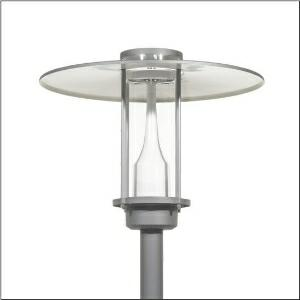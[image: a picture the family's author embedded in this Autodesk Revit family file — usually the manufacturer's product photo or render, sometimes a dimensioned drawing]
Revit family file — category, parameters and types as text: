
# Revit family: city-light_plus_iq___pl1_2s_5xa5275jf14h_3179
name_source: partatom
category: Lighting Fixtures
units: mm (PartAtom-declared; Revit-internal decimal feet)

## family parameters
Cut with Voids When Loaded = No
Host = Face
Light Source = No
Part Type = Normal
Room Calculation Point = No
Round Connector Dimension = Use Diameter
Shared = No

## types (1)
- --- (1 x LED, 2830 lm, 19.3 W, 3000K)
    Apparent Load = 19 VA
    CIE Flux Codes = 23 63 93 97 100
    Color Rendering = 70
    Color Temperature = 3000K
    Default Elevation = 1800 mm
    Description = City-Light Plus iQ, mast luminaire, Module 540 iQ-SR, primary light control with 3 zone facetted reflector, of plastic, silver coated, highly specular, structured, primary optical cover: cover, of PMMA, transparent, light distribution: PL1.2s, light emission: direct distribution, primary light characteristic: symmetric, installation type: post-top, LED, High Power LED, rated luminous flux: 2.830lm, luminous efficacy: 146lm/W, light colour: 730, colour temperature: 3000K, control gear: iQ Street-Remote, control: Auto-Match, Temp-Guard, Lumen-Switch, Night-Set, Smart-Wire, Light-Fading, Desk-Remote (wireless, voltage-free reading and setting of iQ features in the workshop via application-optimized NFC function/RFID function), optimised constant luminous flux control (CLO 2.0), Street-Remote, pre-setting: logarithmic dimming characteristic, with terminal, 6-pole, max. 2.5mm², mains connection: 230..240V, AC, 50/60Hz, start of lifetime: 19W, end of service life: 21W, reduction: 10W, luminaire housing, upper part, of glass-fibre reinforced polyester, coated, Siteco® metallic grey (DB 702S), diameter: 750mm, height: 590mm, spigot size: d x l = 76 x 70mm (post-top) | with reducer (optional accessory) 60 x 70mm, mounting height: 3..5m, post-top mast mounting element, of diecast aluminium, coated, Siteco® metallic grey (DB 702S), Module 540 iQ-SR, traffic white (RAL 9016), equipment: standard, protection rating (complete): IP65, insulation class (complete): insulation class II (safety insulation), certification: CE, ENEC, VDE, packaging unit: 1 piece

Light Distribution: PL1.2s
    Height = 590 mm
    Lamp = 1 x LED
    Lamp Light Flux = 2830 lm
    Lamp Power = 19.3 W
    Lamp count = 1
    Length = 750 mm
    Luminous efficacy = 147 lm/W
    Manufacturer = Siteco
    ModVariant = No
    Model = 5XA5275JF14H
    Number of Poles = 1
    OnlyDefault = Yes
    Power Factor = 1
    Product Name = City-Light Plus iQ | PL1.2s
    Product group = mast luminaire | pylon top
    ProductGroupID = 6100
    Protection Class = Protection class II
    Protection Degree = IP 65
    RLX_Detail_Level = 1
    RLX_Emergency_Light_Flux = 0 lm
    RLX_Emergency_Type = 0
    RLX_Emergency_Type_DB = No
    RlxData = <blob elided: 33197 chars, md5=d89eeebc>
    Socket = socket
    Standby Power = 0 W
    System Light Flux = 2830 lm
    System Power = 19 W
    Type Comments = factory setting: luminous flux: 100 % | dim-lin: 254 | 403 mA
    Type Image = l_1006456.jpg
    URL = http://relux.com
    VarID = @adj_167037
    Voltage = 0 V
    Weight = 0.00 kg
    Width = 0 mm  [stored 0 ft]

note: [stored X ft] marks values corroborated as IEEE doubles in the binary element streams (Revit-internal decimal feet)

## geometry (parser evidence)
native form markers: Blend x4, Sweep x12
no freeform markers — native parametric forms only
